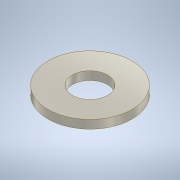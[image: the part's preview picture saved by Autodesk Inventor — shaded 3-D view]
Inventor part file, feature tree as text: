
AUTODESK INVENTOR PART (.ipt)
format: ipt  version: 2020.2 (Build 242310000, 310)  size: 96,768 bytes
history: native  units: mm
features: other x1, extrude x1, sketch x1
ambient origin geometry x8: Origin, YZ Plane, XZ Plane, XY Plane, X Axis, Y Axis, Z Axis, Center Point
bodies: Body1 (feature_tree)
feature tree (3):
  other  "ソリッド1"
  extrude  "押し出し1"  Depth=10.0mm
  sketch  "スケッチ1"
